# Revit family: BTSMP-OMNI
name_source: partatom
category: Communication Devices
revit_build: Autodesk Revit 2014 (Build: 20130308_1515(x64)
units: mm (PartAtom-declared; Revit-internal decimal feet)

## types (1)
- BTSMP-OMNI
    Assembly Code = D5090
    Certifications = Conforms with UL STD 508, UL STD 244A
• OMNI-O: IP65 Rated
    Default Elevation = 48 "
    Description = • Passive Infrared (PIR) sensing technology provides excellent major
motion detection
• Wireless programming using HCS controlHUBB mobile app
• 0-10V dimming control
• Single/Dual motion sensor timer modes
• Daylight sensor with multiple daylight harvesting modes
    Housing Material = Paint - Hubbell - Matte White
    Manufacturer = Hubbell Control Solutions
    Model = Bluetooth® OMNI Sensor Module
    Mounting = :2.75 (Mounting Height : Coverage Radius);
Up to 14ft
    Power Requirements = Low Voltage sensors: 12-32VDC (Requires
Dim to Off driver with auxiliary power or low
voltage power supply - Not included)
    Product Documentation Link = https://hubbellcdn.com
    Product Page URL = https://www.hubbell.com
    Sensing Element = Paint - Hubbell - Gray Smooth
    Type Comments = Bluetooth® OMNI Sensor Module
    URL = https://www.hubbell.com
    Warranty = 5-Years Warranty

## geometry (parser evidence)
native form markers: Sweep x1
no freeform markers — native parametric forms only
